# Revit family: PK-AF
name_source: partatom
category: Duct Accessories
units: mm (PartAtom-declared; Revit-internal decimal feet)

## family parameters
Always vertical = Yes
Cut with Voids When Loaded = No
Part Type = Attaches To
Round Connector Dimension = Use Diameter
Shared = No
Work Plane-Based = No

## types (11) — shared parameters
00_20_Manufacturer = BLAUBERG
00_20_Name = Roof adapter
Casing Material = Metal, painted, grey, matt RAL 7040
Load Classification = HVAC
M = 52 mm
Maintenance zone material = <By Category>
Manufacturer = BLAUBERG
zero-valued in all types: Default Elevation

## per-type parameters (varying)
| type | A | B | D2 | Diameter | Dn | Dy | H | Height | K | Length | Weight | Width | h | k |
| PK-AF-400 | 580 mm  [stored 1.90289 ft] | 701 mm | 490 mm  [stored 1.60761 ft] | 400 mm  [stored 1.31234 ft] | 410 mm  [stored 1.34514 ft] | 400 mm  [stored 1.31234 ft] | 170 mm  [stored 0.557743 ft] | 170 mm  [stored 0.557743 ft] | 217 mm | 701 mm | 17.50 kg | 701 mm | 20 mm  [stored 0.0656168 ft] | 205 mm  [stored 0.672572 ft] |
| PK-AF-450 | 580 mm  [stored 1.90289 ft] | 701 mm | 540 mm  [stored 1.77165 ft] | 450 mm  [stored 1.47638 ft] | 460 mm  [stored 1.50919 ft] | 450 mm  [stored 1.47638 ft] | 170 mm  [stored 0.557743 ft] | 170 mm  [stored 0.557743 ft] | 197 mm | 701 mm | 16.50 kg | 701 mm | 20 mm  [stored 0.0656168 ft] | 230 mm  [stored 0.754593 ft] |
| PK-AF-1250 | 1500 mm | 1700 mm | 1400 mm | 1250 mm | 1260 mm | 1250 mm | 340 mm  [stored 1.11549 ft] | 340 mm  [stored 1.11549 ft] | 376 mm | 1700 mm | 107.00 kg | 1700 mm | 40 mm  [stored 0.131234 ft] | 630 mm |
| PK-AF-1120 | 1340 mm | 1510 mm | 1270 mm | 1120 mm | 1130 mm | 1120 mm | 340 mm  [stored 1.11549 ft] | 340 mm  [stored 1.11549 ft] | 333 mm  [stored 1.09252 ft] | 1510 mm | 91.30 kg | 1510 mm | 40 mm  [stored 0.131234 ft] | 565 mm  [stored 1.85367 ft] |
| PK-AF-500 | 640 mm | 770 mm | 600 mm | 500 mm  [stored 1.64042 ft] | 510 mm  [stored 1.67323 ft] | 500 mm  [stored 1.64042 ft] | 170 mm  [stored 0.557743 ft] | 170 mm  [stored 0.557743 ft] | 211 mm  [stored 0.692257 ft] | 770 mm | 20.30 kg | 770 mm | 20 mm  [stored 0.0656168 ft] | 255 mm  [stored 0.836614 ft] |
| PK-AF-560 | 750 mm | 920 mm | 660 mm | 560 mm  [stored 1.83727 ft] | 570 mm  [stored 1.87008 ft] | 560 mm  [stored 1.83727 ft] | 170 mm  [stored 0.557743 ft] | 170 mm  [stored 0.557743 ft] | 262 mm  [stored 0.85958 ft] | 920 mm | 27.20 kg | 920 mm | 20 mm  [stored 0.0656168 ft] | 285 mm  [stored 0.935039 ft] |
| PK-AF-630 | 750 mm | 920 mm | 730 mm | 630 mm | 640 mm | 630 mm | 170 mm  [stored 0.557743 ft] | 170 mm  [stored 0.557743 ft] | 234 mm  [stored 0.767717 ft] | 920 mm | 25.50 kg | 920 mm | 20 mm  [stored 0.0656168 ft] | 320 mm  [stored 1.04987 ft] |
| PK-AF-710 | 980 mm | 1150 mm | 810 mm | 710 mm | 720 mm | 710 mm | 290 mm  [stored 0.951444 ft] | 290 mm  [stored 0.951444 ft] | 317 mm | 1150 mm | 53.00 kg | 1150 mm | 40 mm  [stored 0.131234 ft] | 360 mm  [stored 1.1811 ft] |
| PK-AF-800 | 980 mm | 1150 mm | 900 mm | 800 mm | 810 mm | 800 mm | 290 mm  [stored 0.951444 ft] | 290 mm  [stored 0.951444 ft] | 281 mm  [stored 0.921916 ft] | 1150 mm | 51.10 kg | 1150 mm | 40 mm  [stored 0.131234 ft] | 405 mm |
| PK-AF-900 | 1050 mm | 1220 mm | 1015 mm | 900 mm | 910 mm | 900 mm | 290 mm  [stored 0.951444 ft] | 290 mm  [stored 0.951444 ft] | 276 mm | 1220 mm | 54.50 kg | 1220 mm | 40 mm  [stored 0.131234 ft] | 455 mm |
| PK-AF-1000 | 1340 mm | 1510 mm | 1115 mm | 1000 mm | 1010 mm | 1000 mm | 340 mm  [stored 1.11549 ft] | 340 mm  [stored 1.11549 ft] | 381 mm  [stored 1.25 ft] | 1510 mm | 93.40 kg | 1510 mm | 40 mm  [stored 0.131234 ft] | 505 mm  [stored 1.65682 ft] |

note: column(s) folded — value = type name in every type: 00_20_Type

note: [stored X ft] marks values corroborated as IEEE doubles in the binary element streams (Revit-internal decimal feet)
